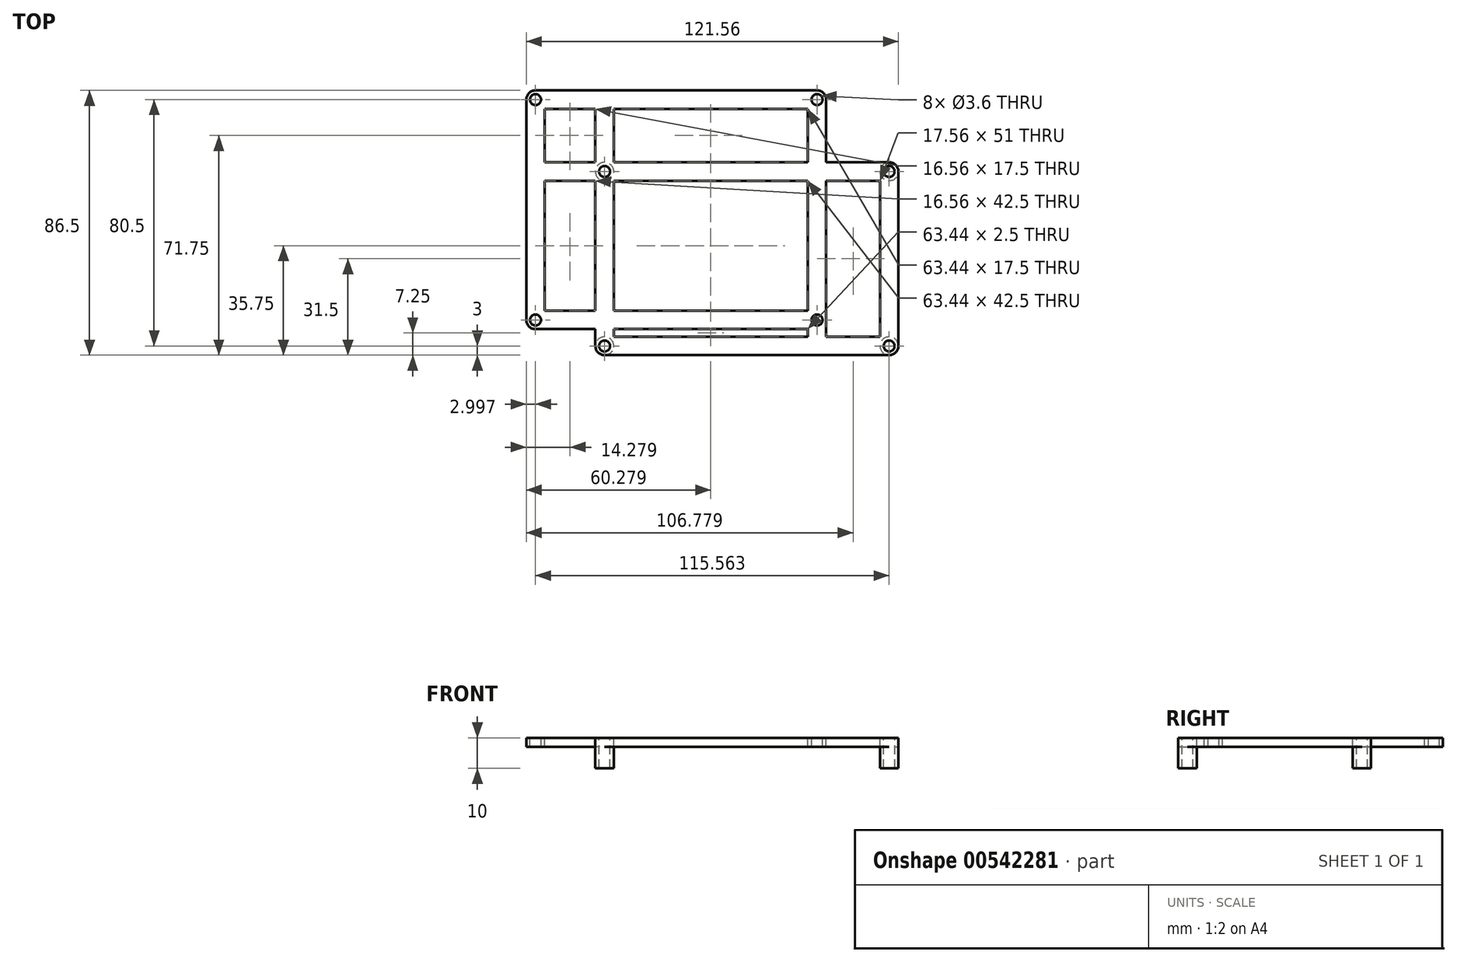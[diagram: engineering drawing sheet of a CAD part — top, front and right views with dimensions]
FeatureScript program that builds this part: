
annotation { "Feature Type Name" : "Feature", "Feature Type Description" : "" }
export const myFeature = defineFeature(function(context is Context, id is Id, definition is map)
    precondition{}
    {
        {
            var Q0;
            Q0=qCreatedBy(makeId("Top.planeOp"),FACE);
            var sketch = newSketch(context, id + "F0", { "sketchPlane" : qUnion([Q0])});
            skLineSegment(sketch, "E0.bottom", {"start": v(-46.5, 28.5) * mm, "end": v(46.5, 28.5) * mm, "construction": true});
            skLineSegment(sketch, "E0.top", {"start": v(-46.5, -28.5) * mm, "end": v(46.5, -28.5) * mm, "construction": true});
            skLineSegment(sketch, "E0.left", {"start": v(-46.5, 28.5) * mm, "end": v(-46.5, -28.5) * mm, "construction": true});
            skLineSegment(sketch, "E0.right", {"start": v(46.5, 28.5) * mm, "end": v(46.5, -28.5) * mm, "construction": true});
            skPoint(sketch, "E0.middle", {"position": v(0, 0) * mm});
            skCircle(sketch, "E1", {"center": v(-46.5, 28.5) * mm, "radius": 1.8 * mm});
            skCircle(sketch, "E2", {"center": v(-46.5, -28.5) * mm, "radius": 1.8 * mm});
            skCircle(sketch, "E3", {"center": v(46.5, -28.5) * mm, "radius": 1.8 * mm});
            skCircle(sketch, "E4", {"center": v(46.5, 28.5) * mm, "radius": 1.8 * mm});
            skCircle(sketch, "E5", {"center": v(-46.5, 28.5) * mm, "radius": 3 * mm});
            skCircle(sketch, "E6", {"center": v(-46.5, -28.5) * mm, "radius": 3 * mm});
            skCircle(sketch, "E7", {"center": v(46.5, -28.5) * mm, "radius": 3 * mm});
            skCircle(sketch, "E8", {"center": v(46.5, 28.5) * mm, "radius": 3 * mm});
            skLineSegment(sketch, "E9", {"start": v(0, 0) * mm, "end": v(0, 52) * mm, "construction": true});
            skPoint(sketch, "E9.endSnap0", {"position": v(0, 28.5) * mm});
            skLineSegment(sketch, "E10.bottom", {"start": v(22.94, 52) * mm, "end": v(-69.06, 52) * mm, "construction": true});
            skLineSegment(sketch, "E10.top", {"start": v(22.94, -20) * mm, "end": v(-69.06, -20) * mm, "construction": true});
            skLineSegment(sketch, "E10.left", {"start": v(22.94, 52) * mm, "end": v(22.94, -20) * mm, "construction": true});
            skLineSegment(sketch, "E10.right", {"start": v(-69.06, 52) * mm, "end": v(-69.06, -20) * mm, "construction": true});
            skCircle(sketch, "E11", {"center": v(-69.06, 52) * mm, "radius": 3 * mm});
            skCircle(sketch, "E12", {"center": v(-69.06, -20) * mm, "radius": 3 * mm});
            skCircle(sketch, "E13", {"center": v(22.94, 52) * mm, "radius": 3 * mm});
            skCircle(sketch, "E14", {"center": v(22.94, -20) * mm, "radius": 3 * mm});
            skCircle(sketch, "E15", {"center": v(22.94, 52) * mm, "radius": 1.8 * mm});
            skCircle(sketch, "E16", {"center": v(22.94, -20) * mm, "radius": 1.8 * mm});
            skCircle(sketch, "E17", {"center": v(-69.06, -20) * mm, "radius": 1.8 * mm});
            skCircle(sketch, "E18", {"center": v(-69.06, 52) * mm, "radius": 1.8 * mm});
            skLineSegment(sketch, "E19", {"start": v(-69.06, 55) * mm, "end": v(22.94, 55) * mm});
            skLineSegment(sketch, "E20", {"start": v(-69.06, -23) * mm, "end": v(-49.5, -23) * mm});
            skLineSegment(sketch, "E21", {"start": v(25.94, -25.5) * mm, "end": v(25.94, -20) * mm});
            skLineSegment(sketch, "E22", {"start": v(46.5, 31.5) * mm, "end": v(25.94, 31.5) * mm});
            skLineSegment(sketch, "E23", {"start": v(-49.5, 25.5) * mm, "end": v(-49.5, -17) * mm});
            skLineSegment(sketch, "E24", {"start": v(-46.5, -31.5) * mm, "end": v(19.94, -31.5) * mm});
            skLineSegment(sketch, "E25", {"start": v(49.5, -28.5) * mm, "end": v(49.5, 28.5) * mm});
            skLineSegment(sketch, "E26", {"start": v(19.94, 49) * mm, "end": v(-66.06, 49) * mm});
            skLineSegment(sketch, "E27", {"start": v(-72.06, 52) * mm, "end": v(-72.06, -20) * mm});
            skLineSegment(sketch, "E28", {"start": v(-66.06, 49) * mm, "end": v(-66.06, -17) * mm});
            skLineSegment(sketch, "E29", {"start": v(-66.06, -17) * mm, "end": v(-49.5, -17) * mm});
            skLineSegment(sketch, "E30", {"start": v(19.94, -25.5) * mm, "end": v(19.94, -23) * mm});
            skLineSegment(sketch, "E31", {"start": v(-43.5, 25.5) * mm, "end": v(19.94, 25.5) * mm});
            skLineSegment(sketch, "E32", {"start": v(-43.5, 25.5) * mm, "end": v(-43.5, -17) * mm});
            skLineSegment(sketch, "E33", {"start": v(-43.5, -25.5) * mm, "end": v(19.94, -25.5) * mm});
            skLineSegment(sketch, "E34", {"start": v(43.5, -25.5) * mm, "end": v(43.5, 25.5) * mm});
            skPoint(sketch, "E35.orphan", {"position": v(43.5, 28.5) * mm});
            skLineSegment(sketch, "E36.trimOffspring", {"start": v(19.94, 31.5) * mm, "end": v(19.94, 49) * mm});
            skLineSegment(sketch, "E37.trimOffspring", {"start": v(25.94, 31.5) * mm, "end": v(25.94, 52) * mm});
            skLineSegment(sketch, "E38.trimOffspring", {"start": v(19.94, 31.5) * mm, "end": v(-43.5, 31.5) * mm});
            skLineSegment(sketch, "E39.trimOffspring", {"start": v(25.94, 25.5) * mm, "end": v(43.5, 25.5) * mm});
            skPoint(sketch, "E40.orphan", {"position": v(-69.06, 49) * mm});
            skPoint(sketch, "E41.orphan", {"position": v(22.94, -17) * mm});
            skLineSegment(sketch, "E42.trimOffspring", {"start": v(25.94, -25.5) * mm, "end": v(25.94, 25.5) * mm});
            skLineSegment(sketch, "E43.trimOffspring", {"start": v(25.94, -25.5) * mm, "end": v(43.5, -25.5) * mm});
            skLineSegment(sketch, "E44.trimOffspring", {"start": v(25.94, -31.5) * mm, "end": v(46.5, -31.5) * mm});
            skPoint(sketch, "E45.orphan", {"position": v(-43.5, -28.5) * mm});
            skLineSegment(sketch, "E46", {"start": v(19.94, -31.5) * mm, "end": v(25.94, -31.5) * mm});
            skLineSegment(sketch, "E47.trimOffspring", {"start": v(19.94, -17) * mm, "end": v(19.94, 25.5) * mm});
            skPoint(sketch, "E48.orphan", {"position": v(22.94, -23) * mm});
            skLineSegment(sketch, "E49.trimOffspring", {"start": v(-43.5, -23) * mm, "end": v(-43.5, -25.5) * mm});
            skLineSegment(sketch, "E50.trimOffspring", {"start": v(-49.5, -23) * mm, "end": v(-49.5, -28.5) * mm});
            skLineSegment(sketch, "E51.trimOffspring", {"start": v(-43.5, -17) * mm, "end": v(19.94, -17) * mm});
            skLineSegment(sketch, "E52.trimOffspring", {"start": v(-43.5, -23) * mm, "end": v(19.94, -23) * mm});
            skLineSegment(sketch, "E53", {"start": v(-49.5, 25.5) * mm, "end": v(-66.06, 25.5) * mm});
            skLineSegment(sketch, "E54", {"start": v(-49.5, 31.5) * mm, "end": v(-66.06, 31.5) * mm});
            skLineSegment(sketch, "E55", {"start": v(-49.5, 31.5) * mm, "end": v(-49.5, 49) * mm});
            skLineSegment(sketch, "E56", {"start": v(-43.5, 31.5) * mm, "end": v(-43.5, 49) * mm});
            skPoint(sketch, "E57.orphan", {"position": v(-49.5, 28.5) * mm});
            skPoint(sketch, "E58.orphan", {"position": v(-46.5, 31.5) * mm});
            skSolve(sketch);
        }
        {
            var Q0;
            Q0=makeQuery(id+"F0.imprint","IMPRINT",FACE,{"disambiguationData":[TD([[makeQuery(id+"F0.imprint","IMPRINT",EDGE,{"derivedFrom":sQuery(id+"F0.wireOp",EDGE,"E17")}),-1.0]])]});
            var Q1;
            Q1=makeQuery(id+"F0.imprint","IMPRINT",FACE,{"disambiguationData":[TD([[makeQuery(id+"F0.imprint","IMPRINT",EDGE,{"derivedFrom":sQuery(id+"F0.wireOp",EDGE,"E14")}),1.0]])]});
            var Q2;
            Q2=makeQuery(id+"F0.imprint","IMPRINT",FACE,{"disambiguationData":[TD([[makeQuery(id+"F0.imprint","IMPRINT",EDGE,{"derivedFrom":sQuery(id+"F0.wireOp",EDGE,"E15")}),-1.0]])]});
            var Q3;
            Q3=makeQuery(id+"F0.imprint","IMPRINT",FACE,{"disambiguationData":[TD([[makeQuery(id+"F0.imprint","IMPRINT",EDGE,{"derivedFrom":sQuery(id+"F0.wireOp",EDGE,"E18")}),-1.0]])]});
            var Q4;
            {var subQ22=sQuery(id+"F0.wireOp",EDGE,"E14");Q4=makeQuery(id+"F0.imprint","IMPRINT",FACE,{"disambiguationData":[TD([[makeQuery(id+"F0.imprint","IMPRINT",EDGE,{"derivedFrom":subQ22}),-1.0]])]});}
            extrude(context, id + "F1", {"entities" : qUnion([Q0, Q1, Q2, Q3, Q4]), "oppositeDirection" : true, "depth" : 3 * mm, "offsetDistance" : 25 * mm});
        }
        {
            var Q0;
            Q0=makeQuery(id+"F0.imprint","IMPRINT",FACE,{"disambiguationData":[TD([[makeQuery(id+"F0.imprint","IMPRINT",EDGE,{"derivedFrom":sQuery(id+"F0.wireOp",EDGE,"E4")}),-1.0]])]});
            var Q1;
            Q1=makeQuery(id+"F0.imprint","IMPRINT",FACE,{"disambiguationData":[TD([[makeQuery(id+"F0.imprint","IMPRINT",EDGE,{"derivedFrom":sQuery(id+"F0.wireOp",EDGE,"E3")}),-1.0]])]});
            var Q2;
            Q2=makeQuery(id+"F0.imprint","IMPRINT",FACE,{"disambiguationData":[TD([[makeQuery(id+"F0.imprint","IMPRINT",EDGE,{"derivedFrom":sQuery(id+"F0.wireOp",EDGE,"E2")}),-1.0]])]});
            var Q3;
            Q3=makeQuery(id+"F0.imprint","IMPRINT",FACE,{"disambiguationData":[TD([[makeQuery(id+"F0.imprint","IMPRINT",EDGE,{"derivedFrom":sQuery(id+"F0.wireOp",EDGE,"E1")}),-1.0]])]});
            extrude(context, id + "F2", {"entities" : qUnion([Q0, Q1, Q2, Q3]), "operationType" : NewBodyOperationType.ADD, "oppositeDirection" : true, "depth" : 10 * mm, "offsetDistance" : 25 * mm});
        }
    });
